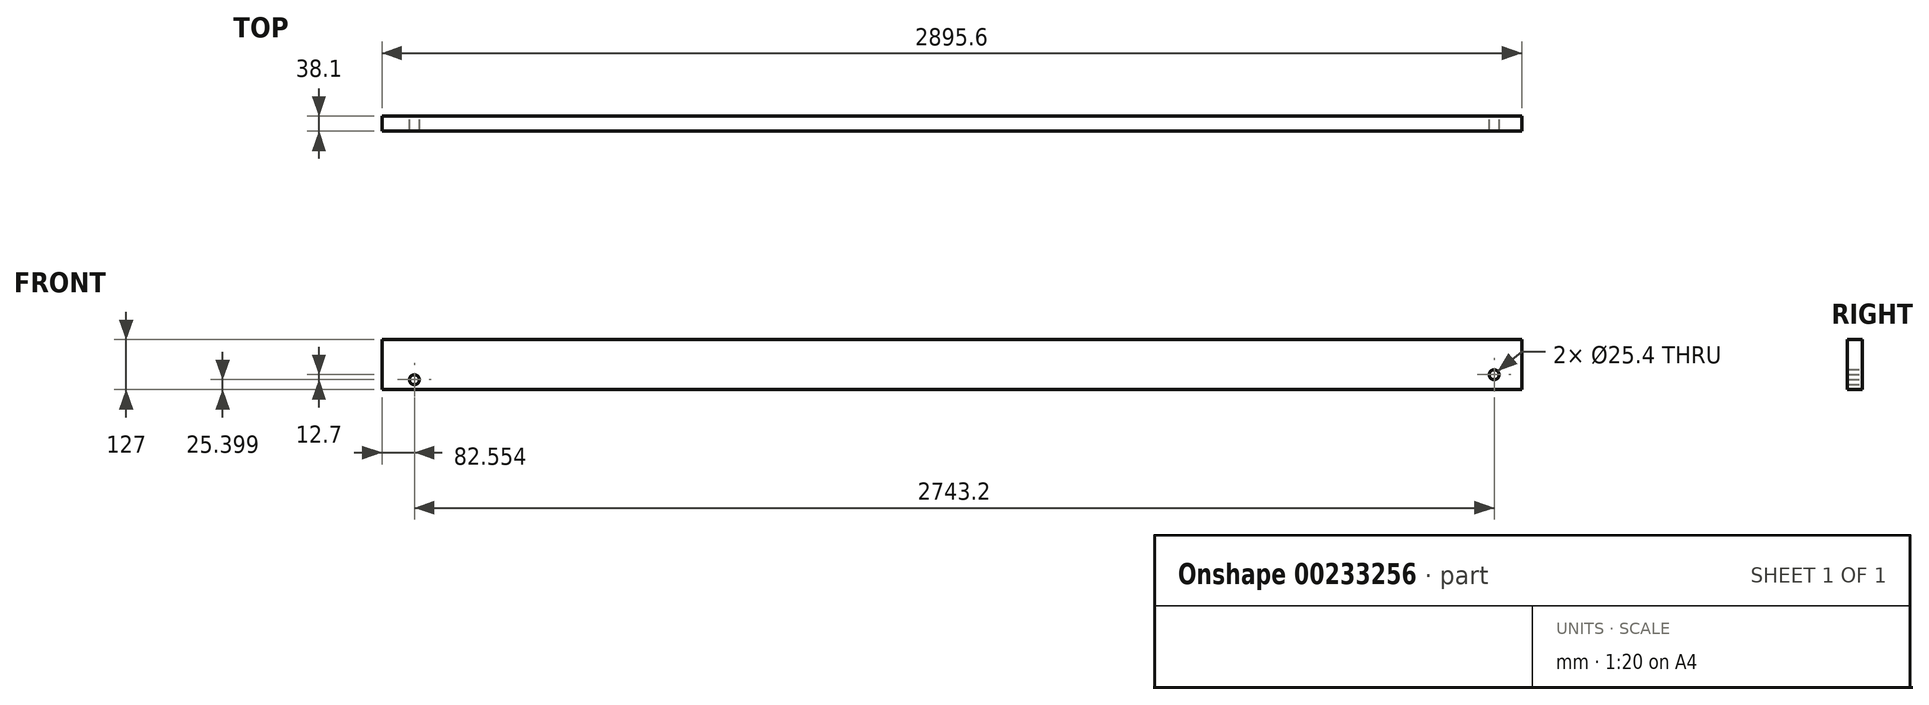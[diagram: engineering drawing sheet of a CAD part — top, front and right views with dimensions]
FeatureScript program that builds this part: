
annotation { "Feature Type Name" : "Feature", "Feature Type Description" : "" }
export const myFeature = defineFeature(function(context is Context, id is Id, definition is map)
    precondition{}
    {
        {
            var Q0;
            Q0=qCreatedBy(makeId("Front.planeOp"),FACE);
            var sketch = newSketch(context, id + "F0", { "sketchPlane" : qUnion([Q0])});
            skLineSegment(sketch, "E0.bottom", {"start": v(-1422.06, -48.66) * mm, "end": v(1473.54, -48.66) * mm});
            skLineSegment(sketch, "E0.top", {"start": v(-1422.06, -175.66) * mm, "end": v(1473.54, -175.66) * mm});
            skLineSegment(sketch, "E0.left", {"start": v(-1422.06, -48.66) * mm, "end": v(-1422.06, -175.66) * mm});
            skLineSegment(sketch, "E0.right", {"start": v(1473.54, -48.66) * mm, "end": v(1473.54, -175.66) * mm});
            skCircle(sketch, "E1", {"center": v(-1339.5, -150.26) * mm, "radius": 12.7 * mm});
            skCircle(sketch, "E2", {"center": v(1403.7, -137.56) * mm, "radius": 12.7 * mm});
            skSolve(sketch);
        }
        {
            var Q0;
            Q0 = qSketchRegion(id + "F0", true);
            extrude(context, id + "F1", {"entities" : qUnion([Q0]), "depth" : 38.1 * mm});
        }
    });
